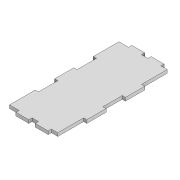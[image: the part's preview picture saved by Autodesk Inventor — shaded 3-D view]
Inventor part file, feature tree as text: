
AUTODESK INVENTOR PART (.ipt)
format: ipt  version: 2022 (Build 260153000, 153)  size: 131,584 bytes
history: native  units: mm
features: extrude x1, sketch x1
ambient origin geometry x8: Origin, YZ Plane, XZ Plane, XY Plane, X Axis, Y Axis, Z Axis, Center Point
bodies: Solid1 (feature_tree)
feature tree (2):
  extrude  "Extrusion1"  Depth=70.0mm
  sketch  "Sketch1"  dims[d0=170.0mm d1=70.0mm d2=5.0mm d3=30.0mm d4=5.0mm d5=30.0mm d6=30.0mm d7=15.0mm d8=20.0mm d9=20.0mm d10=5.0mm d11=5.0mm d12=10.0mm d13=5.0mm d14=5.0mm d15=0.0mm]
